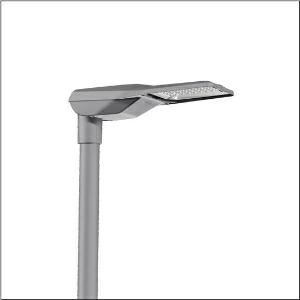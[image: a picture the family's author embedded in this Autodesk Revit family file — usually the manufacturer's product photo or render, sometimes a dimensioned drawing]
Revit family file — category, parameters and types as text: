
# Revit family: streetlight_sl_21_iq_mini___st0_8a_5xe2c41g08gb_95af
name_source: partatom
category: Lighting Fixtures
units: mm (PartAtom-declared; Revit-internal decimal feet)

## family parameters
Cut with Voids When Loaded = No
Host = Face
Light Source = No
Part Type = Normal
Room Calculation Point = No
Round Connector Dimension = Use Diameter
Shared = No

## types (1)
- --- (1 x LED, 5920 lm, 37.1 W, 4000K)
    Apparent Load = 37 VA
    CIE Flux Codes = 38 75 97 100 100
    Color Rendering = 70
    Color Temperature = 4000K
    Default Elevation = 1800 mm
    Description = Streetlight SL 21 iQ mini, mast luminaire, primary light control with lens, of PMMA, primary optical cover: cover, of toughened safety glass, transparent, light distribution: ST0.8a, light emission: direct distribution, primary light characteristic: asymmetric, installation type: post-top, side-entry, LED, High Power LED, rated luminous flux: 5.920lm, luminous efficacy: 160lm/W, light colour: 740, colour temperature: 4000K, control: Street-Remote, Auto-Match, Temp-Guard, Lumen-Switch, Night-Set, Smart-Wire, Light-Fading, Desk-Remote (wireless, voltage-free reading and setting of iQ features in the workshop via application-optimized NFC function/RFID function), optimised constant luminous flux control (CLO 2.0), pre-setting: linear dimming characteristic, mains connection: 220..240V, AC, 50/60Hz, start of lifetime: 37W, end of service life: 39W, reduction: 18W, luminaire housing, of diecast aluminium, powder-coated, Siteco® metallic grey (DB 702S), corrosivity category C5 mid according to DIN EN ISO 12944, please order mast flange separately, inclination adjustable: 0°, 5°, 10°, 15°, sealing non-destructively replaceable, multi-level sealing system, length: 628mm, width: 235mm, height: 110mm, mast flange for spigot size: 42mm (side-entry): 5XC10008XM4, 60/48mm (side-entry/post-top): 5XC10108XM2, 76/60mm (side-entry/post-top): 5XC10108XM1, protection rating (complete): IP66, insulation class (complete): insulation class II (safety insulation), certification: CE, ENEC, ENEC+, VDE, impact resistance: IK09, permissible operating ambient temperature for outdoor applications: -40..+50°C, standard-compliant lighting for roads and squares, packaging unit: 1 piece

Light Distribution: ST0.8a
    Height = 110 mm
    Lamp = 1 x LED
    Lamp Light Flux = 5920 lm
    Lamp Power = 37.1 W
    Lamp count = 1
    Length = 625 mm
    Luminous efficacy = 160 lm/W
    Manufacturer = Siteco
    ModVariant = No
    Model = 5XE2C41G08GB
    Number of Poles = 1
    OnlyDefault = Yes
    Power Factor = 1
    Product Name = Streetlight SL 21 iQ mini | ST0.8a
    Product group = mast luminaire | pylon top
    ProductGroupID = 6100
    Protection Class = Protection class II
    Protection Degree = IP 66
    RLX_Detail_Level = 1
    RLX_Emergency_Light_Flux = 0 lm
    RLX_Emergency_Type = 0
    RLX_Emergency_Type_DB = No
    RlxData = <blob elided: 93661 chars, md5=05f0971e>
    Socket = socket
    Standby Power = 0 W
    System Light Flux = 5920 lm
    System Power = 37 W
    Type Comments = factory setting: luminous flux: 100 % | dim-lin: 254 | 385 mA
    Type Image = l_1003519.jpg
    URL = http://relux.com
    VarID = @adj_157261
    Voltage = 0 V
    Weight = 0.00 kg
    Width = 234 mm

## geometry (parser evidence)
native form markers: Blend x4, Sweep x11
no freeform markers — native parametric forms only
